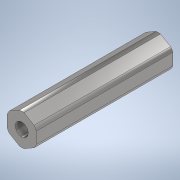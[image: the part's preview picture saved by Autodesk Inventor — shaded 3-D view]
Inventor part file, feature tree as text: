
AUTODESK INVENTOR PART (.ipt)
format: ipt  version: 2020 (Build 240168000, 168)  size: 117,248 bytes
history: native  units: in
note: dims shown in document units (in); Inventor stores cm internally (conversion verified against a paired STEP export)
features: extrude x1, sketch x1
ambient origin geometry x8: Origin, YZ Plane, XZ Plane, XY Plane, X Axis, Y Axis, Z Axis, Center Point
bodies: Solid1 (feature_tree)
feature tree (2):
  extrude  "Extrusion1"  Depth=1.75in TaperAngle=0.0deg
  sketch  "Sketch1"  dims[d0=0.375in d1=1.75in d2=0.0in d6=0.4035in d7=0.165in]
